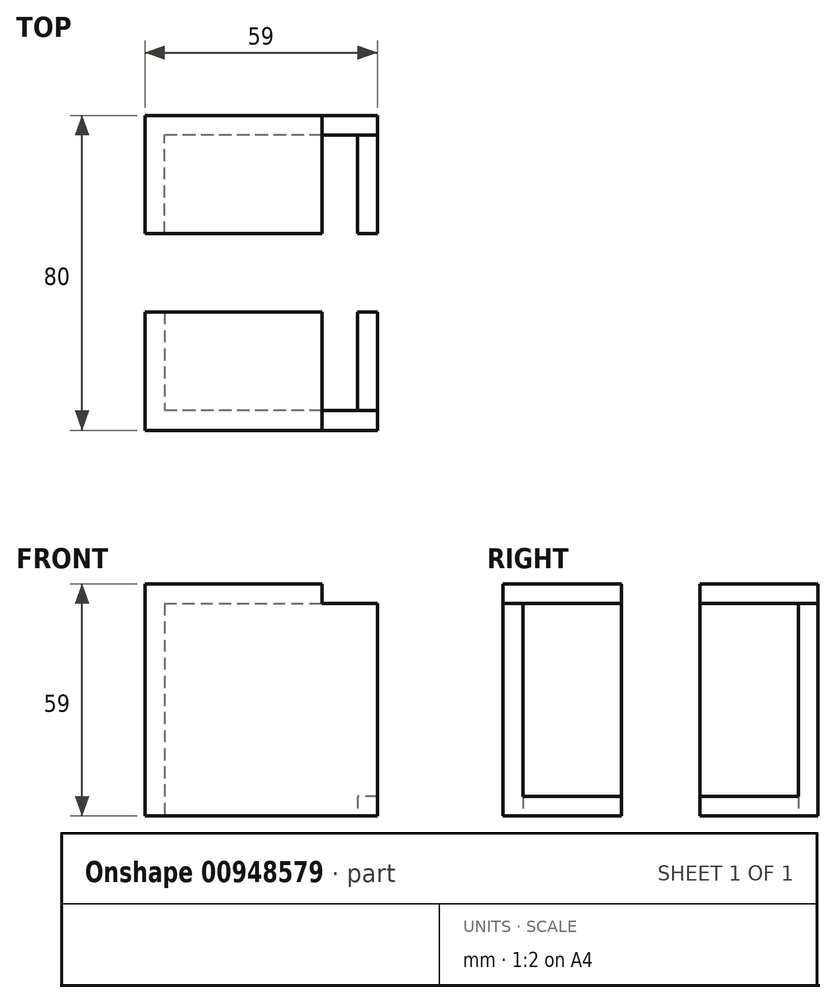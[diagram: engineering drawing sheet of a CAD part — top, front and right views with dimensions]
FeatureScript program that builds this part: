
annotation { "Feature Type Name" : "Feature", "Feature Type Description" : "" }
export const myFeature = defineFeature(function(context is Context, id is Id, definition is map)
    precondition{}
    {
        {
            var Q0;
            Q0=qCreatedBy(makeId("Top.planeOp"),FACE);
            var sketch = newSketch(context, id + "F0", { "sketchPlane" : qUnion([Q0])});
            skLineSegment(sketch, "E0.bottom", {"start": v(0, 0) * mm, "end": v(59, 0) * mm});
            skLineSegment(sketch, "E0.top", {"start": v(0, -30) * mm, "end": v(59, -30) * mm});
            skLineSegment(sketch, "E0.left", {"start": v(0, 0) * mm, "end": v(0, -30) * mm});
            skLineSegment(sketch, "E0.right", {"start": v(59, 0) * mm, "end": v(59, -30) * mm});
            skSolve(sketch);
        }
        {
            var Q0;
            Q0=makeQuery(id+"F0.imprint","IMPRINT",FACE,{"disambiguationData":[TD([[makeQuery(id+"F0.imprint","IMPRINT",EDGE,{"derivedFrom":sQuery(id+"F0.wireOp",EDGE,"E0.bottom")}),-1.0]])]});
            extrude(context, id + "F1", {"entities" : qUnion([Q0]), "depth" : 59 * mm, "offsetDistance" : 25.4 * mm});
        }
        {
            var Q0;
            Q0=makeQuery(id+"F1.opExtrude","CAP_FACE",FACE,{"disambiguationData":[OSD([sQuery(id+"F0.wireOp",EDGE,"E0.bottom"),sQuery(id+"F0.wireOp",EDGE,"E0.top"),sQuery(id+"F0.wireOp",EDGE,"E0.left"),sQuery(id+"F0.wireOp",EDGE,"E0.right")])],"isStart":true});
            var sketch = newSketch(context, id + "F2", { "sketchPlane" : qUnion([Q0])});
            skLineSegment(sketch, "E1.bottom", {"start": v(54, 0) * mm, "end": v(5, 0) * mm});
            skLineSegment(sketch, "E1.top", {"start": v(54, 25) * mm, "end": v(5, 25) * mm});
            skLineSegment(sketch, "E1.left", {"start": v(54, 0) * mm, "end": v(54, 25) * mm});
            skLineSegment(sketch, "E1.right", {"start": v(5, 0) * mm, "end": v(5, 25) * mm});
            skSolve(sketch);
        }
        {
            var Q0;
            Q0=makeQuery(id+"F2.imprint","IMPRINT",FACE,{"disambiguationData":[TD([[makeQuery(id+"F2.imprint","IMPRINT",EDGE,{"derivedFrom":sQuery(id+"F2.wireOp",EDGE,"E1.bottom")}),1.0]])]});
            extrude(context, id + "F3", {"entities" : qUnion([Q0]), "operationType" : NewBodyOperationType.REMOVE, "oppositeDirection" : true, "depth" : 54 * mm, "offsetDistance" : 25 * mm});
        }
        {
            var Q0;
            Q0=makeQuery(id+"F3.boolean.opBoolean","COPY",FACE,{"derivedFrom":makeQuery(id+"F3.opExtrude","SWEPT_FACE",FACE,{"disambiguationData":[OSD([sQuery(id+"F2.wireOp",EDGE,"E1.left")])]})});
            var sketch = newSketch(context, id + "F4", { "sketchPlane" : qUnion([Q0])});
            skLineSegment(sketch, "E2.bottom", {"start": v(25, 54) * mm, "end": v(0, 54) * mm});
            skLineSegment(sketch, "E2.top", {"start": v(25, 5) * mm, "end": v(0, 5) * mm});
            skLineSegment(sketch, "E2.left", {"start": v(25, 54) * mm, "end": v(25, 5) * mm});
            skLineSegment(sketch, "E2.right", {"start": v(0, 54) * mm, "end": v(0, 5) * mm});
            skSolve(sketch);
        }
        {
            var Q0;
            Q0 = qSketchRegion(id + "F4", true);
            extrude(context, id + "F5", {"entities" : qUnion([Q0]), "operationType" : NewBodyOperationType.REMOVE, "depth" : -5 * mm, "offsetDistance" : 25 * mm});
        }
        {
            var Q0;
            {var subQ2=sQuery(id+"F0.wireOp",EDGE,"E0.left");var subQ4=sQuery(id+"F0.wireOp",EDGE,"E0.bottom");Q0=makeQuery(id+"F5.boolean.opBoolean","SPLIT",FACE,{"disambiguationData":[TD([makeQuery(id+"F1.opExtrude","SWEPT_FACE",FACE,{"disambiguationData":[OSD([subQ2])]})])],"derivedFrom":makeQuery(id+"F1.opExtrude","SWEPT_FACE",FACE,{"disambiguationData":[OSD([subQ4])]})});}
            var sketch = newSketch(context, id + "F6", { "sketchPlane" : qUnion([Q0])});
            skLineSegment(sketch, "E3.bottom", {"start": v(-59, 54) * mm, "end": v(-45, 54) * mm});
            skLineSegment(sketch, "E3.top", {"start": v(-59, 59) * mm, "end": v(-45, 59) * mm});
            skLineSegment(sketch, "E3.left", {"start": v(-59, 54) * mm, "end": v(-59, 59) * mm});
            skLineSegment(sketch, "E3.right", {"start": v(-45, 54) * mm, "end": v(-45, 59) * mm});
            skSolve(sketch);
        }
        {
            var Q0;
            Q0=makeQuery(id+"F6.imprint","IMPRINT",FACE,{"disambiguationData":[TD([[makeQuery(id+"F6.imprint","IMPRINT",EDGE,{"derivedFrom":sQuery(id+"F6.wireOp",EDGE,"E3.bottom")}),-1.0]])]});
            extrude(context, id + "F7", {"entities" : qUnion([Q0]), "operationType" : NewBodyOperationType.REMOVE, "oppositeDirection" : true, "depth" : 30 * mm, "offsetDistance" : 25 * mm});
        }
        {
            var Q0;
            Q0=qCreatedBy(makeId("Front.planeOp"),FACE);
            cPlane(context, id + "F8", {"entities" : qUnion([Q0]), "cplaneType" : CPlaneType.OFFSET, "offset" : 10 * mm, "oppositeDirection" : true, "width" : 150 * mm, "height" : 150 * mm});
        }
        {
            var Q0;
            Q0=makeQuery(id+"F1.opExtrude","SWEPT_BODY",BODY,{"disambiguationData":[OSD([sQuery(id+"F0.wireOp",EDGE,"E0.bottom"),sQuery(id+"F0.wireOp",EDGE,"E0.top"),sQuery(id+"F0.wireOp",EDGE,"E0.left"),sQuery(id+"F0.wireOp",EDGE,"E0.right")])]});
            var Q1;
            Q1=qCreatedBy(id+"F8.planeOp",FACE);
            mirror(context, id + "F9", {"entities" : qUnion([Q0]), "mirrorPlane" : qUnion([Q1])});
        }
    });
